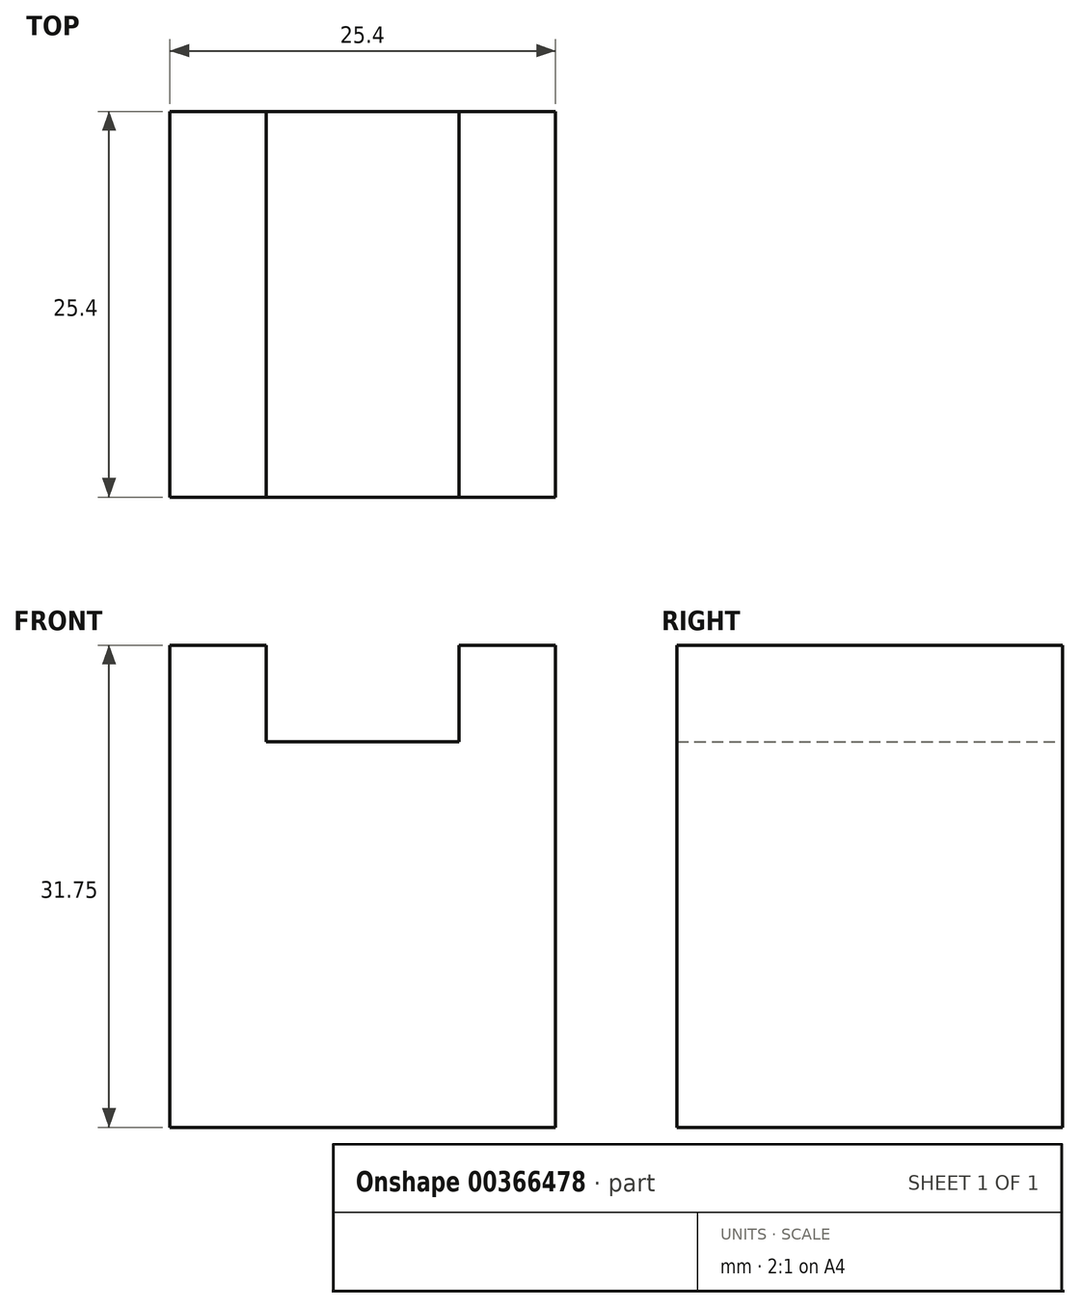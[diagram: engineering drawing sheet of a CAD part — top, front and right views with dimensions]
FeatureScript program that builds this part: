
annotation { "Feature Type Name" : "Feature", "Feature Type Description" : "" }
export const myFeature = defineFeature(function(context is Context, id is Id, definition is map)
    precondition{}
    {
        {
            var Q0;
            Q0=qCreatedBy(makeId("Front.planeOp"),FACE);
            var sketch = newSketch(context, id + "F0", { "sketchPlane" : qUnion([Q0])});
            skLineSegment(sketch, "E0", {"start": v(0, 0) * mm, "end": v(0, 31.75) * mm});
            skLineSegment(sketch, "E1", {"start": v(0, 31.75) * mm, "end": v(6.35, 31.75) * mm});
            skLineSegment(sketch, "E2", {"start": v(6.35, 31.75) * mm, "end": v(6.35, 25.4) * mm});
            skLineSegment(sketch, "E3", {"start": v(6.35, 25.4) * mm, "end": v(19.05, 25.4) * mm});
            skLineSegment(sketch, "E4", {"start": v(19.05, 25.4) * mm, "end": v(19.05, 31.75) * mm});
            skLineSegment(sketch, "E5", {"start": v(19.05, 31.75) * mm, "end": v(25.4, 31.75) * mm});
            skLineSegment(sketch, "E6", {"start": v(25.4, 31.75) * mm, "end": v(25.4, 0) * mm});
            skLineSegment(sketch, "E7", {"start": v(25.4, 0) * mm, "end": v(0, 0) * mm});
            skSolve(sketch);
        }
        {
            var Q0;
            Q0 = qSketchRegion(id + "F0", true);
            extrude(context, id + "F1", {"entities" : qUnion([Q0]), "depth" : 25.4 * mm});
        }
        {
            var Q0;
            Q0 = qSketchRegion(id + "F0", true);
            extrude(context, id + "F2", {"entities" : qUnion([Q0]), "depth" : 25.4 * mm});
        }
        {
            var Q0;
            Q0=qCreatedBy(makeId("Front.planeOp"),FACE);
            var sketch = newSketch(context, id + "F3", { "sketchPlane" : qUnion([Q0])});
            skLineSegment(sketch, "E8", {"start": v(11.21, 0) * mm, "end": v(11.21, 8.23) * mm});
            skLineSegment(sketch, "E9", {"start": v(11.21, 8.23) * mm, "end": v(16.04, 8.23) * mm});
            skLineSegment(sketch, "E10", {"start": v(16.04, 8.23) * mm, "end": v(16.04, 0) * mm});
            skLineSegment(sketch, "E11", {"start": v(16.04, 0) * mm, "end": v(11.21, 0) * mm});
            skSolve(sketch);
        }
        {
            var Q0;
            Q0 = qSketchRegion(id + "F3", true);
            extrude(context, id + "F4", {"entities" : qUnion([Q0]), "operationType" : NewBodyOperationType.REMOVE, "oppositeDirection" : true, "depth" : 25.4 * mm});
        }
    });
